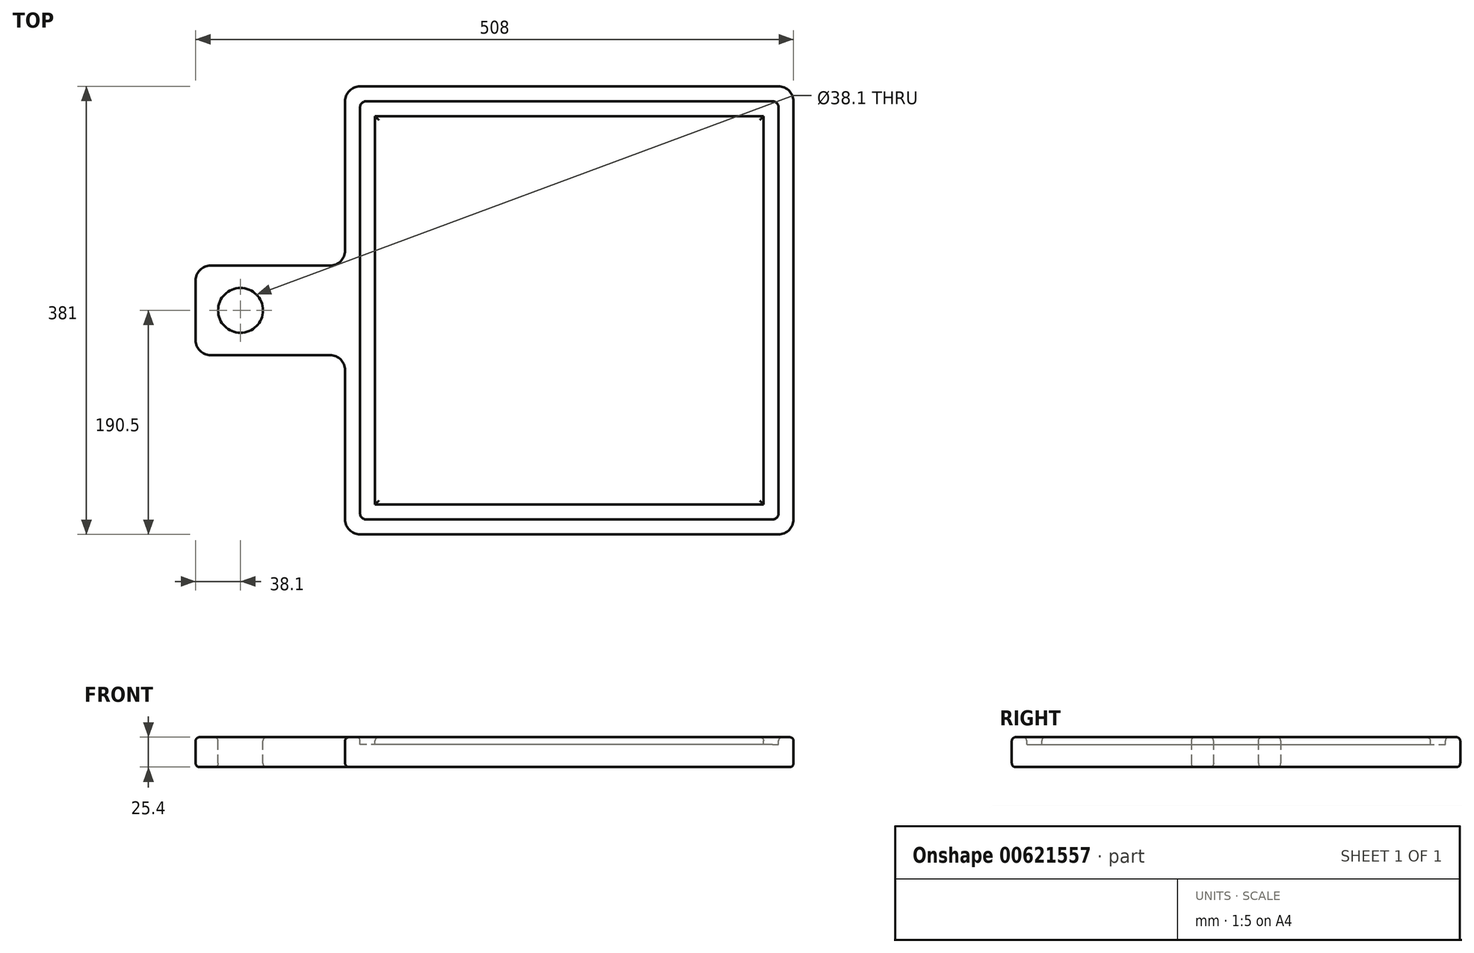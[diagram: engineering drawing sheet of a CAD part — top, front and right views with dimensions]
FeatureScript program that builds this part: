
annotation { "Feature Type Name" : "Feature", "Feature Type Description" : "" }
export const myFeature = defineFeature(function(context is Context, id is Id, definition is map)
    precondition{}
    {
        {
            var Q0;
            Q0=qCreatedBy(makeId("Top.planeOp"),FACE);
            var sketch = newSketch(context, id + "F0", { "sketchPlane" : qUnion([Q0])});
            skLineSegment(sketch, "E0.bottom", {"start": v(0, 0) * mm, "end": v(381, 0) * mm});
            skLineSegment(sketch, "E0.top", {"start": v(0, 381) * mm, "end": v(381, 381) * mm});
            skLineSegment(sketch, "E0.left", {"start": v(0, 0) * mm, "end": v(0, 381) * mm});
            skLineSegment(sketch, "E0.right", {"start": v(381, 0) * mm, "end": v(381, 381) * mm});
            skLineSegment(sketch, "E1.bottom", {"start": v(0, 152.4) * mm, "end": v(-127, 152.4) * mm});
            skLineSegment(sketch, "E1.top", {"start": v(0, 228.6) * mm, "end": v(-127, 228.6) * mm});
            skLineSegment(sketch, "E1.left", {"start": v(0, 152.4) * mm, "end": v(0, 228.6) * mm});
            skLineSegment(sketch, "E1.right", {"start": v(-127, 152.4) * mm, "end": v(-127, 228.6) * mm});
            skSolve(sketch);
        }
        {
            var Q0;
            {var subQ3=sQuery(id+"F0.wireOp",EDGE,"E0.bottom");Q0=makeQuery(id+"F0.imprint","IMPRINT",FACE,{"disambiguationData":[TD([[makeQuery(id+"F0.imprint","IMPRINT",EDGE,{"derivedFrom":subQ3}),1.0]])]});}
            var Q1;
            Q1=makeQuery(id+"F0.imprint","IMPRINT",FACE,{"disambiguationData":[TD([[makeQuery(id+"F0.imprint","IMPRINT",EDGE,{"derivedFrom":sQuery(id+"F0.wireOp",EDGE,"E1.bottom")}),-1.0]])]});
            extrude(context, id + "F1", {"entities" : qUnion([Q0, Q1]), "depth" : 25.4 * mm, "offsetDistance" : 25.4 * mm});
        }
        {
            var Q0;
            Q0=makeQuery(id+"F1.opExtrude","CAP_FACE",FACE,{"disambiguationData":[OSD([sQuery(id+"F0.wireOp",EDGE,"E0.bottom"),sQuery(id+"F0.wireOp",EDGE,"E0.top"),sQuery(id+"F0.wireOp",EDGE,"E0.left"),sQuery(id+"F0.wireOp",EDGE,"E0.right"),sQuery(id+"F0.wireOp",EDGE,"E1.bottom"),sQuery(id+"F0.wireOp",EDGE,"E1.top"),sQuery(id+"F0.wireOp",EDGE,"E1.right")])],"isStart":false});
            var sketch = newSketch(context, id + "F2", { "sketchPlane" : qUnion([Q0])});
            skCircle(sketch, "E2", {"center": v(-88.9, 190.5) * mm, "radius": 19.05 * mm});
            skPoint(sketch, "E2.centerSnap0", {"position": v(-127, 190.5) * mm});
            skSolve(sketch);
        }
        {
            var Q0;
            Q0 = qSketchRegion(id + "F2", true);
            extrude(context, id + "F3", {"entities" : qUnion([Q0]), "operationType" : NewBodyOperationType.REMOVE, "oppositeDirection" : true, "depth" : 25.4 * mm, "offsetDistance" : 25.4 * mm});
        }
        {
            var Q0;
            Q0=makeQuery(id+"F2.imprint","IMPRINT",FACE,{"disambiguationData":[TD([[makeQuery(id+"F2.imprint","IMPRINT",EDGE,{"derivedFrom":sQuery(id+"F2.wireOp",EDGE,"E2")}),-1.0]])]});
            var sketch = newSketch(context, id + "F4", { "sketchPlane" : qUnion([Q0])});
            skLineSegment(sketch, "E3.0", {"start": v(368.3, 368.3) * mm, "end": v(12.7, 368.3) * mm});
            skLineSegment(sketch, "E3.1", {"start": v(368.3, 12.7) * mm, "end": v(368.3, 368.3) * mm});
            skLineSegment(sketch, "E3.2", {"start": v(12.7, 368.3) * mm, "end": v(12.7, 215.9) * mm});
            skLineSegment(sketch, "E3.3", {"start": v(12.7, 12.7) * mm, "end": v(368.3, 12.7) * mm});
            skLineSegment(sketch, "E3.7", {"start": v(12.7, 165.1) * mm, "end": v(12.7, 12.7) * mm});
            skLineSegment(sketch, "E4", {"start": v(12.7, 215.9) * mm, "end": v(12.7, 165.1) * mm});
            skLineSegment(sketch, "E5.0", {"start": v(355.6, 25.4) * mm, "end": v(355.6, 355.6) * mm});
            skLineSegment(sketch, "E5.1", {"start": v(25.4, 355.6) * mm, "end": v(25.4, 215.9) * mm});
            skLineSegment(sketch, "E5.2", {"start": v(25.4, 215.9) * mm, "end": v(25.4, 165.1) * mm});
            skLineSegment(sketch, "E5.3", {"start": v(355.6, 355.6) * mm, "end": v(25.4, 355.6) * mm});
            skLineSegment(sketch, "E5.4", {"start": v(25.4, 165.1) * mm, "end": v(25.4, 25.4) * mm});
            skLineSegment(sketch, "E5.5", {"start": v(25.4, 25.4) * mm, "end": v(355.6, 25.4) * mm});
            skSolve(sketch);
        }
        {
            var Q0;
            Q0=makeQuery(id+"F4.imprint","IMPRINT",FACE,{"disambiguationData":[TD([[makeQuery(id+"F4.imprint","IMPRINT",EDGE,{"derivedFrom":sQuery(id+"F4.wireOp",EDGE,"E3.0")}),1.0]])]});
            extrude(context, id + "F5", {"entities" : qUnion([Q0]), "operationType" : NewBodyOperationType.REMOVE, "oppositeDirection" : true, "depth" : 6.35 * mm, "offsetDistance" : 25.4 * mm});
        }
        {
            var Q0;
            Q0=makeQuery(id+"F5.boolean.opBoolean","COPY",EDGE,{"derivedFrom":makeQuery(id+"F5.opExtrude","SWEPT_EDGE",EDGE,{"disambiguationData":[OSD([sQuery(id+"F4.wireOp",EDGE,"E3.0"),sQuery(id+"F4.wireOp",EDGE,"E3.2")])]})});
            var Q1;
            Q1=makeQuery(id+"F5.boolean.opBoolean","COPY",EDGE,{"derivedFrom":makeQuery(id+"F5.opExtrude","SWEPT_EDGE",EDGE,{"disambiguationData":[OSD([sQuery(id+"F4.wireOp",EDGE,"E3.0"),sQuery(id+"F4.wireOp",EDGE,"E3.1")])]})});
            var Q2;
            Q2=makeQuery(id+"F5.boolean.opBoolean","COPY",EDGE,{"derivedFrom":makeQuery(id+"F5.opExtrude","SWEPT_EDGE",EDGE,{"disambiguationData":[OSD([sQuery(id+"F4.wireOp",EDGE,"E3.3"),sQuery(id+"F4.wireOp",EDGE,"E3.7")])]})});
            var Q3;
            Q3=makeQuery(id+"F5.boolean.opBoolean","COPY",EDGE,{"derivedFrom":makeQuery(id+"F5.opExtrude","SWEPT_EDGE",EDGE,{"disambiguationData":[OSD([sQuery(id+"F4.wireOp",EDGE,"E3.1"),sQuery(id+"F4.wireOp",EDGE,"E3.3")])]})});
            fillet(context, id + "F6", {"entities" : qUnion([Q0, Q1, Q2, Q3]), "radius" : 5.08 * mm, "tangentPropagation" : true, "allowEdgeOverflow" : false});
        }
        {
            var Q0;
            Q0=makeQuery(id+"F1.opExtrude","SWEPT_EDGE",EDGE,{"disambiguationData":[OSD([sQuery(id+"F0.wireOp",EDGE,"E0.bottom"),sQuery(id+"F0.wireOp",EDGE,"E0.right")])]});
            var Q1;
            Q1=makeQuery(id+"F1.opExtrude","SWEPT_EDGE",EDGE,{"disambiguationData":[OSD([sQuery(id+"F0.wireOp",EDGE,"E0.bottom"),sQuery(id+"F0.wireOp",EDGE,"E0.left")])]});
            var Q2;
            Q2=makeQuery(id+"F1.opExtrude","SWEPT_EDGE",EDGE,{"disambiguationData":[OSD([sQuery(id+"F0.wireOp",EDGE,"E1.bottom"),sQuery(id+"F0.wireOp",EDGE,"E1.right")])]});
            var Q3;
            Q3=makeQuery(id+"F1.opExtrude","SWEPT_EDGE",EDGE,{"disambiguationData":[OSD([sQuery(id+"F0.wireOp",EDGE,"E0.top"),sQuery(id+"F0.wireOp",EDGE,"E0.right")])]});
            var Q4;
            Q4=makeQuery(id+"F1.opExtrude","SWEPT_EDGE",EDGE,{"disambiguationData":[OSD([sQuery(id+"F0.wireOp",EDGE,"E1.top"),sQuery(id+"F0.wireOp",EDGE,"E1.right")])]});
            var Q5;
            Q5=makeQuery(id+"F1.opExtrude","SWEPT_EDGE",EDGE,{"disambiguationData":[OSD([sQuery(id+"F0.wireOp",EDGE,"E0.top"),sQuery(id+"F0.wireOp",EDGE,"E0.left")])]});
            var Q6;
            Q6=makeQuery(id+"F1.opExtrude","SWEPT_EDGE",EDGE,{"disambiguationData":[OSD([sQuery(id+"F0.wireOp",EDGE,"E0.left"),sQuery(id+"F0.wireOp",EDGE,"E1.top"),sQuery(id+"F0.wireOp",EDGE,"E1.left")])]});
            var Q7;
            Q7=makeQuery(id+"F1.opExtrude","SWEPT_EDGE",EDGE,{"disambiguationData":[OSD([sQuery(id+"F0.wireOp",EDGE,"E0.left"),sQuery(id+"F0.wireOp",EDGE,"E1.bottom"),sQuery(id+"F0.wireOp",EDGE,"E1.left")])]});
            fillet(context, id + "F7", {"entities" : qUnion([Q0, Q1, Q2, Q3, Q4, Q5, Q6, Q7]), "radius" : 12.7 * mm, "tangentPropagation" : true, "allowEdgeOverflow" : false});
        }
        {
            var Q0;
            Q0=makeQuery(id+"F5.boolean.opBoolean","SPLIT",FACE,{"disambiguationData":[TD([makeQuery(id+"F5.opExtrude","SWEPT_FACE",FACE,{"disambiguationData":[OSD([sQuery(id+"F4.wireOp",EDGE,"E5.0")])]})])],"derivedFrom":makeQuery(id+"F1.opExtrude","CAP_FACE",FACE,{"disambiguationData":[OSD([sQuery(id+"F0.wireOp",EDGE,"E0.bottom"),sQuery(id+"F0.wireOp",EDGE,"E0.top"),sQuery(id+"F0.wireOp",EDGE,"E0.left"),sQuery(id+"F0.wireOp",EDGE,"E0.right"),sQuery(id+"F0.wireOp",EDGE,"E1.bottom"),sQuery(id+"F0.wireOp",EDGE,"E1.top"),sQuery(id+"F0.wireOp",EDGE,"E1.right")])],"isStart":false})});
            var Q1;
            {var subQ0=sQuery(id+"F0.wireOp",EDGE,"E1.right");var subQ1=sQuery(id+"F0.wireOp",EDGE,"E1.top");var subQ2=sQuery(id+"F0.wireOp",EDGE,"E1.bottom");var subQ3=sQuery(id+"F0.wireOp",EDGE,"E0.right");var subQ4=sQuery(id+"F0.wireOp",EDGE,"E0.bottom");var subQ5=sQuery(id+"F0.wireOp",EDGE,"E0.left");var subQ6=sQuery(id+"F0.wireOp",EDGE,"E0.top");Q1=makeQuery(id+"F5.boolean.opBoolean","SPLIT",FACE,{"disambiguationData":[TD([makeQuery(id+"F1.opExtrude","SWEPT_FACE",FACE,{"disambiguationData":[OSD([subQ4])]})])],"derivedFrom":makeQuery(id+"F1.opExtrude","CAP_FACE",FACE,{"disambiguationData":[OSD([subQ4,subQ6,subQ5,subQ3,subQ2,subQ1,subQ0])],"isStart":false})});}
            var Q2;
            Q2=makeQuery(id+"F1.opExtrude","SWEPT_FACE",FACE,{"disambiguationData":[OSD([sQuery(id+"F0.wireOp",EDGE,"E0.top")])]});
            var Q3;
            Q3=makeQuery(id+"F7.opFillet","BLEND_FACE",FACE,{"disambiguationData":[OSD([sQuery(id+"F0.wireOp",EDGE,"E0.top"),sQuery(id+"F0.wireOp",EDGE,"E0.left")])]});
            var Q4;
            {var subQ0=sQuery(id+"F0.wireOp",EDGE,"E0.left");var subQ1=sQuery(id+"F0.wireOp",EDGE,"E1.left");var subQ2=sQuery(id+"F0.wireOp",EDGE,"E1.top");Q4=makeQuery(id+"F7.opFillet","BLEND_EDGE",EDGE,{"blendedFrom":[makeQuery(id+"F1.opExtrude","SWEPT_EDGE",EDGE,{"disambiguationData":[OSD([subQ0,subQ2,subQ1])]}),makeQuery(id+"F1.opExtrude","SWEPT_FACE",FACE,{"disambiguationData":[OSD([subQ0]),TDD([makeQuery(id+"F0.imprint","IMPRINT",EDGE,{"disambiguationData":[TD([[makeQuery(id+"F0.imprint","INTERSECT",VERTEX,{"derivedFrom":[sQuery(id+"F0.wireOp",EDGE,"E0.top"),subQ0]}),1.0]])],"derivedFrom":subQ0})])]})],"blendedInto":[makeQuery(id+"F1.opExtrude","SWEPT_FACE",FACE,{"disambiguationData":[OSD([subQ0]),TDD([makeQuery(id+"F0.imprint","IMPRINT",EDGE,{"disambiguationData":[TD([[makeQuery(id+"F0.imprint","INTERSECT",VERTEX,{"derivedFrom":[sQuery(id+"F0.wireOp",EDGE,"E0.top"),subQ0]}),1.0]])],"derivedFrom":subQ0})])]})]});}
            var Q5;
            Q5=makeQuery(id+"F7.opFillet","BLEND_FACE",FACE,{"disambiguationData":[OSD([sQuery(id+"F0.wireOp",EDGE,"E0.left"),sQuery(id+"F0.wireOp",EDGE,"E1.top"),sQuery(id+"F0.wireOp",EDGE,"E1.left")])]});
            var Q6;
            Q6=makeQuery(id+"F1.opExtrude","SWEPT_FACE",FACE,{"disambiguationData":[OSD([sQuery(id+"F0.wireOp",EDGE,"E1.top")])]});
            var Q7;
            {var subQ0=sQuery(id+"F0.wireOp",EDGE,"E0.left");Q7=makeQuery(id+"F1.opExtrude","SWEPT_FACE",FACE,{"disambiguationData":[OSD([subQ0]),TDD([makeQuery(id+"F0.imprint","IMPRINT",EDGE,{"disambiguationData":[TD([[makeQuery(id+"F0.imprint","INTERSECT",VERTEX,{"derivedFrom":[sQuery(id+"F0.wireOp",EDGE,"E0.bottom"),subQ0]}),-1.0]])],"derivedFrom":subQ0})])]});}
            var Q8;
            Q8=makeQuery(id+"F7.opFillet","BLEND_FACE",FACE,{"disambiguationData":[OSD([sQuery(id+"F0.wireOp",EDGE,"E0.left"),sQuery(id+"F0.wireOp",EDGE,"E1.bottom"),sQuery(id+"F0.wireOp",EDGE,"E1.left")])]});
            var Q9;
            Q9=makeQuery(id+"F1.opExtrude","CAP_EDGE",EDGE,{"disambiguationData":[OSD([sQuery(id+"F0.wireOp",EDGE,"E1.bottom")])],"isStart":false});
            var Q10;
            Q10=makeQuery(id+"F1.opExtrude","CAP_EDGE",EDGE,{"disambiguationData":[OSD([sQuery(id+"F0.wireOp",EDGE,"E0.bottom")])],"isStart":false});
            var Q11;
            Q11=makeQuery(id+"F1.opExtrude","CAP_EDGE",EDGE,{"disambiguationData":[OSD([sQuery(id+"F0.wireOp",EDGE,"E0.top")])],"isStart":true});
            var Q12;
            Q12=makeQuery(id+"F1.opExtrude","CAP_FACE",FACE,{"disambiguationData":[OSD([sQuery(id+"F0.wireOp",EDGE,"E0.bottom"),sQuery(id+"F0.wireOp",EDGE,"E0.top"),sQuery(id+"F0.wireOp",EDGE,"E0.left"),sQuery(id+"F0.wireOp",EDGE,"E0.right"),sQuery(id+"F0.wireOp",EDGE,"E1.bottom"),sQuery(id+"F0.wireOp",EDGE,"E1.top"),sQuery(id+"F0.wireOp",EDGE,"E1.right")])],"isStart":true});
            fillet(context, id + "F8", {"entities" : qUnion([Q0, Q1, Q2, Q3, Q4, Q5, Q6, Q7, Q8, Q9, Q10, Q11, Q12]), "radius" : 3.17 * mm, "tangentPropagation" : true, "allowEdgeOverflow" : false});
        }
    });
